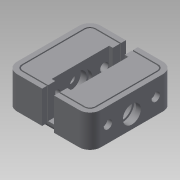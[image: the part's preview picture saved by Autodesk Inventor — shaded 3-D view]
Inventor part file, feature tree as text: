
AUTODESK INVENTOR PART (.ipt)
format: ipt  version: 2015 SP1 (Build 190203100, 203)  size: 331,776 bytes
history: native  units: mm
features: extrude x12, sketch x7, mirror x4, fillet x2, projected_geometry x2, plane x1
ambient origin geometry x8: Origin, YZ Plane, XZ Plane, XY Plane, X Axis, Y Axis, Z Axis, Center Point
bodies: Solid1 (feature_tree)
feature tree (28):
  sketch  "Sketch1"  dims[d0=30.0mm d1=30.0mm]
  extrude  "Extrusion1"  Depth=30.0mm
  extrude  "Extrusion2"  Depth=30.0mm TaperAngle=0.0deg
  extrude  "Extrusion3"  Depth=10.0mm
  sketch  "Sketch2"  dims[d2=3.0mm d3=0.0mm d4=30.0mm d5=0.0mm]
  extrude  "Extrusion6"  Depth=3.5mm
  extrude  "Extrusion7"  Depth=13.5mm TaperAngle=0.0deg
  extrude  "Extrusion8"  Depth=1.5mm
  extrude  "Extrusion9"  Depth=2.0mm
  fillet  "Fillet1"  Radius=2.0mm
  fillet  "Fillet2"  Radius=9.5mm
  plane  "Work Plane1"
  mirror  "Mirror3"
  mirror  "Mirror4"
  extrude  "Extrusion11"  Depth=0.5mm
  extrude  "Extrusion15"  Depth=0.5mm
  extrude  "Extrusion16"  Depth=2.0mm
  mirror  "Mirror7"
  extrude  "Extrusion17"  Depth=2.0mm
  extrude  "Extrusion18"  Depth=27.5mm TaperAngle=0.0deg
  mirror  "Mirror8"
  sketch  "Sketch6"  dims[d6=3.0mm d7=0.0mm d8=10.0mm]
  sketch  "Sketch10"  dims[d9=8.0mm d12=3.5mm]
  sketch  "Sketch11"  dims[d15=11.0mm d16=0.0mm d17=13.5mm d18=0.0mm]
  sketch  "Sketch12"  dims[d19=1.5mm d20=0.0mm d21=8.25mm]
  projected_geometry  "Projected Loop3"
  sketch  "Sketch13"  dims[d22=4.0mm d23=0.0mm d35=2.0mm d36=2.0mm d37=9.5mm d38=0.5mm d39=0.5mm d40=2.0mm d41=2.0mm d42=27.5mm d43=0.0mm d51=5.5mm d52=8.0mm d53=8.0mm d54=0.0mm d55=7.5mm d56=2.0mm d57=0.0mm d61=3.5mm d62=2.0mm d63=0.0mm d64=8.0mm d65=0.0mm]
  projected_geometry  "Projected Loop4"
